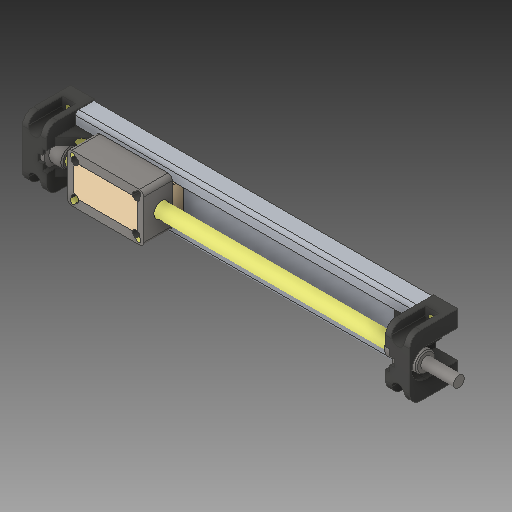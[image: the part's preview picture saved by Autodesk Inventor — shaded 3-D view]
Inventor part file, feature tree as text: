
AUTODESK INVENTOR PART (.ipt)
format: ipt  version: 2019 (Build 230136000, 136)  size: 434,688 bytes
history: native  units: mm
features: extrude x1, sketch x1
ambient origin geometry x8: Origin, YZ Plane, XZ Plane, XY Plane, X Axis, Y Axis, Z Axis, Center Point
bodies: Solid1 (feature_tree), Solid2 (feature_tree)
feature tree (2):
  extrude  "Extrusion1"  Depth=10.0mm
  sketch  "Sketch1"  dims[d0=28.0mm d1=15.0mm d2=3.5mm d3=3.5mm d4=3.5mm d5=3.5mm d6=10.0mm d7=0.0mm]
